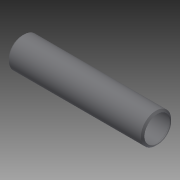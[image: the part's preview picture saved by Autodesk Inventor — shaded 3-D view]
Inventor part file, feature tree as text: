
AUTODESK INVENTOR PART (.ipt)
format: ipt  version: 2014 (Build 180170000, 170)  size: 123,392 bytes
history: native  units: in
note: dims shown in document units (in); Inventor stores cm internally (conversion verified against a paired STEP export)
features: other x56, revolve x1, sketch x1
ambient origin geometry x8: Origin, YZ Plane, XZ Plane, XY Plane, X Axis, Y Axis, Z Axis, Center Point
bodies: Solid1 (feature_tree)
feature tree (58):
  revolve  "Revolution1"  [1 undecoded]
  other  "o1_XY"
  other  "o1_YZ"
  other  "o1_ZX"
  other  "o1_X"
  other  "o1_Y"
  other  "o1_Z"
  other  "o1_Center"
  other  "o2_XY"
  other  "o2_YZ"
  other  "o2_ZX"
  other  "o2_X"
  other  "o2_Y"
  other  "o2_Z"
  other  "o2_Center"
  other  "t1_XY"
  other  "t1_YZ"
  other  "t1_ZX"
  other  "t1_X"
  other  "t1_Y"
  other  "t1_Z"
  other  "t1_Center"
  other  "t2_XY"
  other  "t2_YZ"
  other  "t2_ZX"
  other  "t2_X"
  other  "t2_Y"
  other  "t2_Z"
  other  "t2_Center"
  other  "t3_XY"
  other  "t3_YZ"
  other  "t3_ZX"
  other  "t3_X"
  other  "t3_Y"
  other  "t3_Z"
  other  "t3_Center"
  other  "t4_XY"
  other  "t4_YZ"
  other  "t4_ZX"
  other  "t4_X"
  other  "t4_Y"
  other  "t4_Z"
  other  "t4_Center"
  other  "tube1_XY"
  other  "tube1_YZ"
  other  "tube1_ZX"
  other  "tube1_X"
  other  "tube1_Y"
  other  "tube1_Z"
  other  "tube1_Center"
  other  "tube2_XY"
  other  "tube2_YZ"
  other  "tube2_ZX"
  other  "tube2_X"
  other  "tube2_Y"
  other  "tube2_Z"
  other  "tube2_Center"
  sketch  "Sketch_5"  dims[d0=360.0deg]
note: 1 required parameter value undecoded (feature->parameter linkage not recoverable at this tier; creation-order binding heuristic only, values carry confidence <= 0.55)
